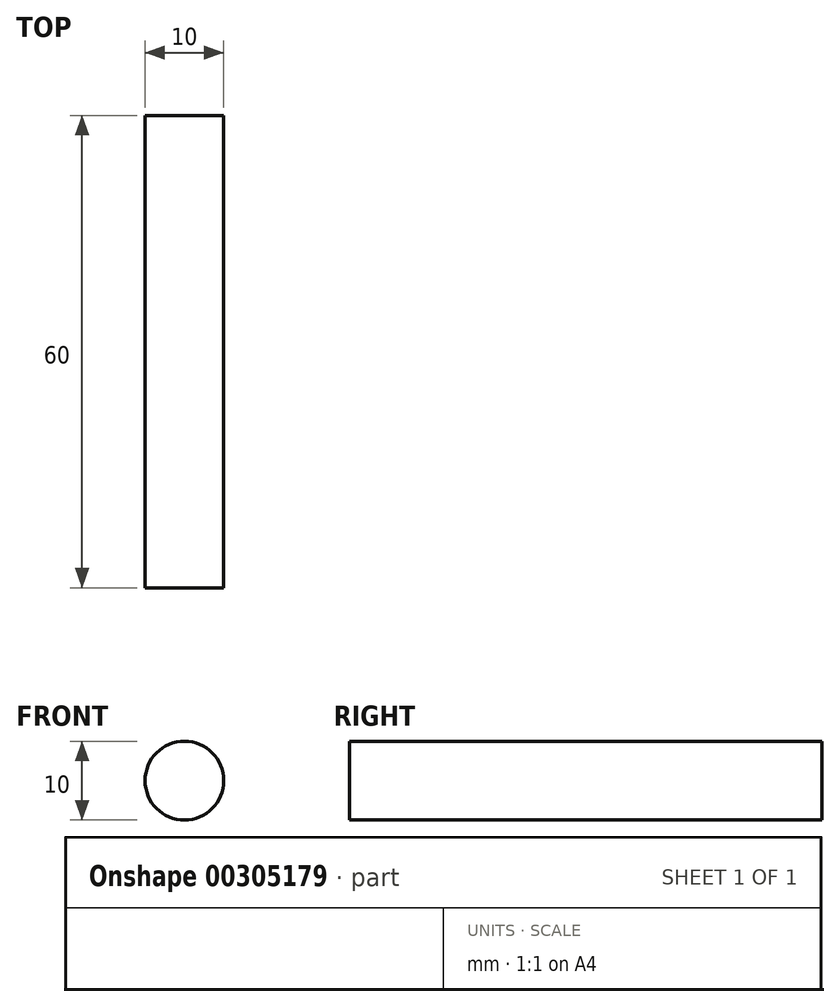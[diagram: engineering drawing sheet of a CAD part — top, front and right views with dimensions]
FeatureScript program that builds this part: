
annotation { "Feature Type Name" : "Feature", "Feature Type Description" : "" }
export const myFeature = defineFeature(function(context is Context, id is Id, definition is map)
    precondition{}
    {
        {
            var Q0;
            Q0=qCreatedBy(makeId("Front.planeOp"),FACE);
            var sketch = newSketch(context, id + "F0", { "sketchPlane" : qUnion([Q0])});
            skCircle(sketch, "E0", {"center": v(0, 0) * mm, "radius": 5 * mm});
            skSolve(sketch);
        }
        {
            var Q0;
            Q0 = qSketchRegion(id + "F0", true);
            extrude(context, id + "F1", {"entities" : qUnion([Q0]), "depth" : 60 * mm, "offsetDistance" : 25 * mm});
        }
    });
